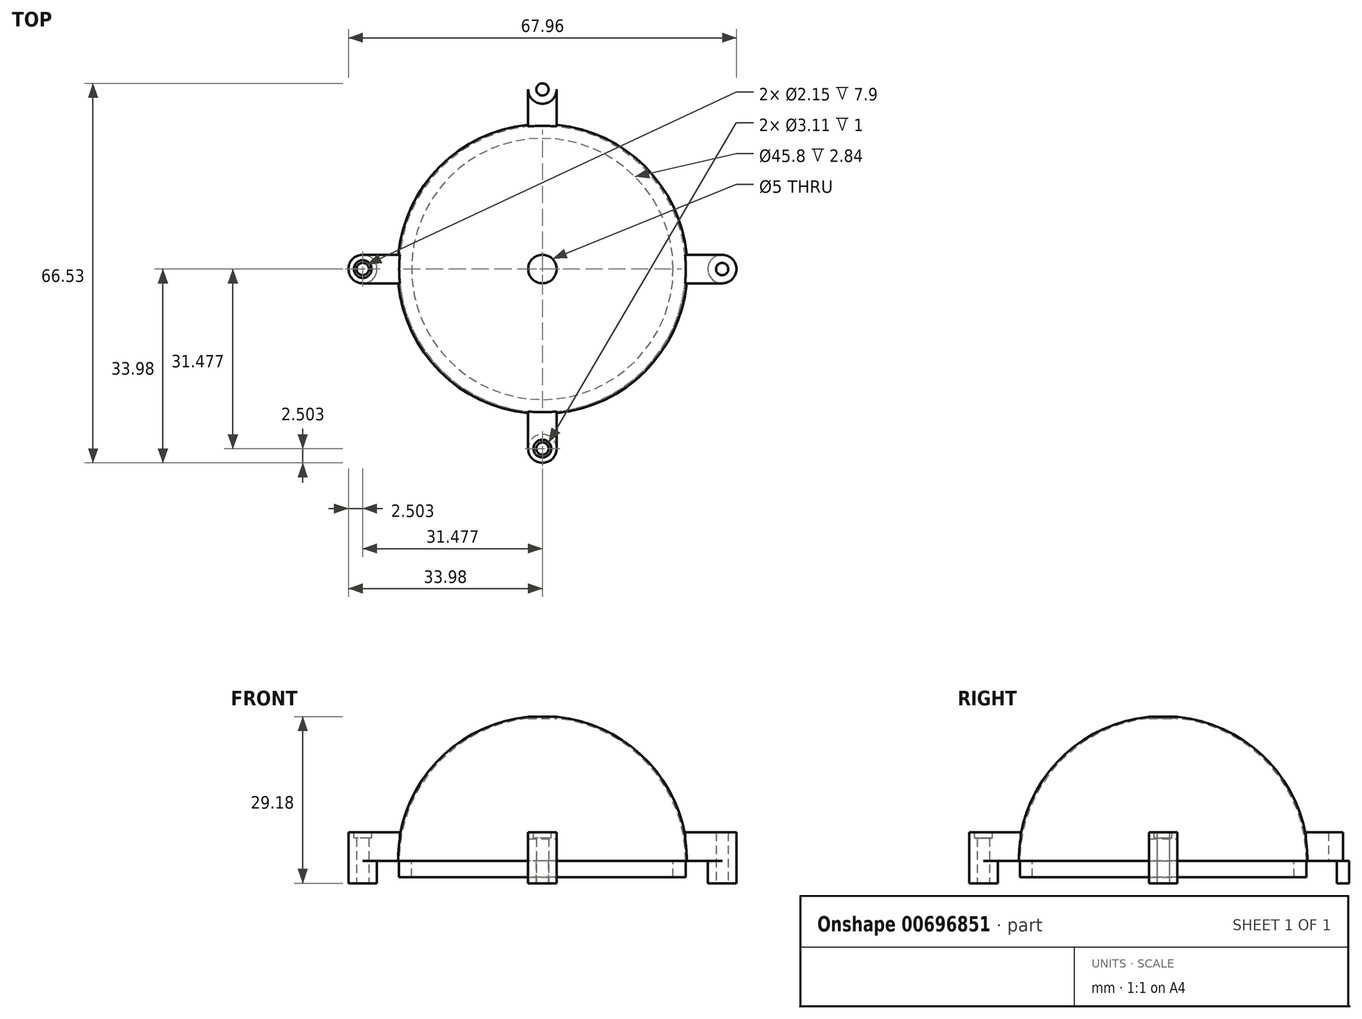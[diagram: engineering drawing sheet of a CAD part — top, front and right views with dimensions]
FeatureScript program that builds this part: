
annotation { "Feature Type Name" : "Feature", "Feature Type Description" : "" }
export const myFeature = defineFeature(function(context is Context, id is Id, definition is map)
    precondition{}
    {
        {
            var Q0;
            Q0=qCreatedBy(makeId("Top.planeOp"),FACE);
            var sketch = newSketch(context, id + "F0", { "sketchPlane" : qUnion([Q0])});
            skCircle(sketch, "E0", {"center": v(0, 0) * mm, "radius": 25.4 * mm});
            skCircle(sketch, "E1", {"center": v(0, 0) * mm, "radius": 22.9 * mm});
            skLineSegment(sketch, "E2", {"start": v(-75.08, 0) * mm, "end": v(76.97, 0) * mm});
            skLineSegment(sketch, "E3", {"start": v(-22.76, 2.5) * mm, "end": v(-31.48, 2.5) * mm});
            skLineSegment(sketch, "E4", {"start": v(-22.76, -2.5) * mm, "end": v(-31.48, -2.5) * mm});
            skCircle(sketch, "E5", {"center": v(-31.48, 0) * mm, "radius": 2.5 * mm});
            skPoint(sketch, "E6", {"position": v(-25.28, 2.5) * mm});
            skLineSegment(sketch, "E7.MirrorCS", {"start": v(22.76, 2.5) * mm, "end": v(31.48, 2.5) * mm});
            skLineSegment(sketch, "E8.MirrorCS", {"start": v(22.76, -2.5) * mm, "end": v(31.48, -2.5) * mm});
            skCircle(sketch, "E9.MirrorC", {"center": v(31.48, 0) * mm, "radius": 2.5 * mm});
            skLineSegment(sketch, "E10", {"start": v(0, 0) * mm, "end": v(95.02, -95.02) * mm, "construction": true});
            skLineSegment(sketch, "E11.MirrorCS", {"start": v(2.5, -22.76) * mm, "end": v(2.5, -31.48) * mm});
            skCircle(sketch, "E12.MirrorC", {"center": v(0, -31.48) * mm, "radius": 2.5 * mm});
            skLineSegment(sketch, "E13.MirrorCS", {"start": v(-2.5, -22.76) * mm, "end": v(-2.5, -31.48) * mm});
            skLineSegment(sketch, "E14.MirrorCS", {"start": v(2.5, 22.76) * mm, "end": v(2.5, 31.48) * mm});
            skCircle(sketch, "E15.MirrorC", {"center": v(0, 31.48) * mm, "radius": 2.5 * mm});
            skLineSegment(sketch, "E16.MirrorCS", {"start": v(-2.5, 22.76) * mm, "end": v(-2.5, 31.48) * mm});
            skCircle(sketch, "E17", {"center": v(0, -31.48) * mm, "radius": 1.07 * mm});
            skCircle(sketch, "E18.MirrorC", {"center": v(31.48, 0) * mm, "radius": 1.07 * mm});
            skCircle(sketch, "E19.MirrorC", {"center": v(0, 31.48) * mm, "radius": 1.07 * mm});
            skCircle(sketch, "E20.MirrorC", {"center": v(-31.48, 0) * mm, "radius": 1.07 * mm});
            skCircle(sketch, "E21", {"center": v(0, 0) * mm, "radius": 25.1 * mm});
            skCircle(sketch, "E22", {"center": v(0, 0) * mm, "radius": 2.5 * mm});
            skSolve(sketch);
        }
        {
            var Q0;
            {var subQ0=sQuery(id+"F0.wireOp",EDGE,"E7.MirrorCS");var subQ1=sQuery(id+"F0.wireOp",EDGE,"E0");var subQ2=makeQuery(id+"F0.imprint","INTERSECT",VERTEX,{"derivedFrom":[subQ1,subQ0]});Q0=makeQuery(id+"F0.imprint","IMPRINT",FACE,{"disambiguationData":[TD([[makeQuery(id+"F0.imprint","IMPRINT",EDGE,{"disambiguationData":[TD([[subQ2,-1.0]])],"derivedFrom":subQ1}),1.0]])]});}
            var Q1;
            {var subQ0=sQuery(id+"F0.wireOp",EDGE,"E7.MirrorCS");var subQ1=sQuery(id+"F0.wireOp",EDGE,"E0");var subQ2=makeQuery(id+"F0.imprint","INTERSECT",VERTEX,{"derivedFrom":[subQ1,subQ0]});Q1=makeQuery(id+"F0.imprint","IMPRINT",FACE,{"disambiguationData":[TD([[makeQuery(id+"F0.imprint","IMPRINT",EDGE,{"disambiguationData":[TD([[subQ2,1.0]])],"derivedFrom":subQ1}),1.0]])]});}
            var Q2;
            {var subQ0=sQuery(id+"F0.wireOp",EDGE,"E14.MirrorCS");var subQ1=sQuery(id+"F0.wireOp",EDGE,"E0");var subQ2=makeQuery(id+"F0.imprint","INTERSECT",VERTEX,{"derivedFrom":[subQ1,subQ0]});Q2=makeQuery(id+"F0.imprint","IMPRINT",FACE,{"disambiguationData":[TD([[makeQuery(id+"F0.imprint","IMPRINT",EDGE,{"disambiguationData":[TD([[subQ2,-1.0]])],"derivedFrom":subQ1}),1.0]])]});}
            var Q3;
            {var subQ0=sQuery(id+"F0.wireOp",EDGE,"E16.MirrorCS");var subQ1=sQuery(id+"F0.wireOp",EDGE,"E0");var subQ2=makeQuery(id+"F0.imprint","INTERSECT",VERTEX,{"derivedFrom":[subQ1,subQ0]});Q3=makeQuery(id+"F0.imprint","IMPRINT",FACE,{"disambiguationData":[TD([[makeQuery(id+"F0.imprint","IMPRINT",EDGE,{"disambiguationData":[TD([[subQ2,-1.0]])],"derivedFrom":subQ1}),1.0]])]});}
            var Q4;
            {var subQ0=sQuery(id+"F0.wireOp",EDGE,"E3");var subQ1=sQuery(id+"F0.wireOp",EDGE,"E0");var subQ2=makeQuery(id+"F0.imprint","INTERSECT",VERTEX,{"derivedFrom":[subQ1,subQ0]});Q4=makeQuery(id+"F0.imprint","IMPRINT",FACE,{"disambiguationData":[TD([[makeQuery(id+"F0.imprint","IMPRINT",EDGE,{"disambiguationData":[TD([[subQ2,-1.0]])],"derivedFrom":subQ1}),1.0]])]});}
            var Q5;
            Q5=sQuery(id+"F0.wireOp",EDGE,"E2");
            revolve(context, id + "F1", {"entities" : qUnion([Q0, Q1, Q2, Q3, Q4]), "axis" : qUnion([Q5]), "revolveType" : RevolveType.ONE_DIRECTION, "angle" : 180 * degree});
        }
        {
            var Q0;
            {var subQ0=sQuery(id+"F0.wireOp",EDGE,"E7.MirrorCS");var subQ1=sQuery(id+"F0.wireOp",EDGE,"E0");var subQ2=makeQuery(id+"F0.imprint","INTERSECT",VERTEX,{"derivedFrom":[subQ1,subQ0]});Q0=makeQuery(id+"F0.imprint","IMPRINT",FACE,{"disambiguationData":[TD([[makeQuery(id+"F0.imprint","IMPRINT",EDGE,{"disambiguationData":[TD([[subQ2,1.0]])],"derivedFrom":subQ1}),-1.0]])]});}
            var Q1;
            {var subQ0=sQuery(id+"F0.wireOp",EDGE,"E8.MirrorCS");var subQ1=sQuery(id+"F0.wireOp",EDGE,"E0");var subQ2=makeQuery(id+"F0.imprint","INTERSECT",VERTEX,{"derivedFrom":[subQ1,subQ0]});Q1=makeQuery(id+"F0.imprint","IMPRINT",FACE,{"disambiguationData":[TD([[makeQuery(id+"F0.imprint","IMPRINT",EDGE,{"disambiguationData":[TD([[subQ2,-1.0]])],"derivedFrom":subQ1}),-1.0]])]});}
            var Q2;
            {var subQ0=sQuery(id+"F0.wireOp",EDGE,"E9.MirrorC");var subQ1=sQuery(id+"F0.wireOp",EDGE,"E2");var subQ2=makeQuery(id+"F0.imprint","INTERSECT",VERTEX,{"disambiguationData":[OD(0.0)],"derivedFrom":[subQ1,subQ0]});Q2=makeQuery(id+"F0.imprint","IMPRINT",FACE,{"disambiguationData":[TD([[makeQuery(id+"F0.imprint","IMPRINT",EDGE,{"disambiguationData":[TD([[subQ2,1.0]])],"derivedFrom":subQ1}),1.0]])]});}
            var Q3;
            {var subQ0=sQuery(id+"F0.wireOp",EDGE,"E9.MirrorC");var subQ1=sQuery(id+"F0.wireOp",EDGE,"E2");var subQ2=makeQuery(id+"F0.imprint","INTERSECT",VERTEX,{"disambiguationData":[OD(0.0)],"derivedFrom":[subQ1,subQ0]});Q3=makeQuery(id+"F0.imprint","IMPRINT",FACE,{"disambiguationData":[TD([[makeQuery(id+"F0.imprint","IMPRINT",EDGE,{"disambiguationData":[TD([[subQ2,1.0]])],"derivedFrom":subQ1}),-1.0]])]});}
            var Q4;
            {var subQ0=sQuery(id+"F0.wireOp",EDGE,"E7.MirrorCS");var subQ1=sQuery(id+"F0.wireOp",EDGE,"E0");var subQ2=makeQuery(id+"F0.imprint","INTERSECT",VERTEX,{"derivedFrom":[subQ1,subQ0]});Q4=makeQuery(id+"F0.imprint","IMPRINT",FACE,{"disambiguationData":[TD([[makeQuery(id+"F0.imprint","IMPRINT",EDGE,{"disambiguationData":[TD([[subQ2,1.0]])],"derivedFrom":subQ1}),1.0]])]});}
            var Q5;
            {var subQ0=sQuery(id+"F0.wireOp",EDGE,"E8.MirrorCS");var subQ1=sQuery(id+"F0.wireOp",EDGE,"E0");var subQ2=makeQuery(id+"F0.imprint","INTERSECT",VERTEX,{"derivedFrom":[subQ1,subQ0]});Q5=makeQuery(id+"F0.imprint","IMPRINT",FACE,{"disambiguationData":[TD([[makeQuery(id+"F0.imprint","IMPRINT",EDGE,{"disambiguationData":[TD([[subQ2,-1.0]])],"derivedFrom":subQ1}),1.0]])]});}
            var Q6;
            {var subQ0=sQuery(id+"F0.wireOp",EDGE,"E14.MirrorCS");var subQ1=sQuery(id+"F0.wireOp",EDGE,"E0");var subQ2=makeQuery(id+"F0.imprint","INTERSECT",VERTEX,{"derivedFrom":[subQ1,subQ0]});Q6=makeQuery(id+"F0.imprint","IMPRINT",FACE,{"disambiguationData":[TD([[makeQuery(id+"F0.imprint","IMPRINT",EDGE,{"disambiguationData":[TD([[subQ2,-1.0]])],"derivedFrom":subQ1}),1.0]])]});}
            var Q7;
            {var subQ0=sQuery(id+"F0.wireOp",EDGE,"E14.MirrorCS");var subQ1=sQuery(id+"F0.wireOp",EDGE,"E0");var subQ2=makeQuery(id+"F0.imprint","INTERSECT",VERTEX,{"derivedFrom":[subQ1,subQ0]});Q7=makeQuery(id+"F0.imprint","IMPRINT",FACE,{"disambiguationData":[TD([[makeQuery(id+"F0.imprint","IMPRINT",EDGE,{"disambiguationData":[TD([[subQ2,-1.0]])],"derivedFrom":subQ1}),-1.0]])]});}
            var Q8;
            {var subQ0=sQuery(id+"F0.wireOp",EDGE,"E15.MirrorC");var subQ1=makeQuery(id+"F0.imprint","INTERSECT",VERTEX,{"derivedFrom":[sQuery(id+"F0.wireOp",EDGE,"E14.MirrorCS"),subQ0]});Q8=makeQuery(id+"F0.imprint","IMPRINT",FACE,{"disambiguationData":[TD([[makeQuery(id+"F0.imprint","IMPRINT",EDGE,{"disambiguationData":[TD([[subQ1,1.0]])],"derivedFrom":subQ0}),-1.0]])]});}
            var Q9;
            {var subQ0=sQuery(id+"F0.wireOp",EDGE,"E3");var subQ1=sQuery(id+"F0.wireOp",EDGE,"E0");var subQ2=makeQuery(id+"F0.imprint","INTERSECT",VERTEX,{"derivedFrom":[subQ1,subQ0]});Q9=makeQuery(id+"F0.imprint","IMPRINT",FACE,{"disambiguationData":[TD([[makeQuery(id+"F0.imprint","IMPRINT",EDGE,{"disambiguationData":[TD([[subQ2,-1.0]])],"derivedFrom":subQ1}),-1.0]])]});}
            var Q10;
            {var subQ0=sQuery(id+"F0.wireOp",EDGE,"E5");var subQ1=sQuery(id+"F0.wireOp",EDGE,"E2");var subQ2=makeQuery(id+"F0.imprint","INTERSECT",VERTEX,{"disambiguationData":[OD(0.0)],"derivedFrom":[subQ1,subQ0]});Q10=makeQuery(id+"F0.imprint","IMPRINT",FACE,{"disambiguationData":[TD([[makeQuery(id+"F0.imprint","IMPRINT",EDGE,{"disambiguationData":[TD([[subQ2,-1.0]])],"derivedFrom":subQ1}),1.0]])]});}
            var Q11;
            {var subQ0=sQuery(id+"F0.wireOp",EDGE,"E5");var subQ1=sQuery(id+"F0.wireOp",EDGE,"E2");var subQ2=makeQuery(id+"F0.imprint","INTERSECT",VERTEX,{"disambiguationData":[OD(0.0)],"derivedFrom":[subQ1,subQ0]});Q11=makeQuery(id+"F0.imprint","IMPRINT",FACE,{"disambiguationData":[TD([[makeQuery(id+"F0.imprint","IMPRINT",EDGE,{"disambiguationData":[TD([[subQ2,-1.0]])],"derivedFrom":subQ1}),-1.0]])]});}
            var Q12;
            {var subQ0=sQuery(id+"F0.wireOp",EDGE,"E4");var subQ1=sQuery(id+"F0.wireOp",EDGE,"E0");var subQ2=makeQuery(id+"F0.imprint","INTERSECT",VERTEX,{"derivedFrom":[subQ1,subQ0]});Q12=makeQuery(id+"F0.imprint","IMPRINT",FACE,{"disambiguationData":[TD([[makeQuery(id+"F0.imprint","IMPRINT",EDGE,{"disambiguationData":[TD([[subQ2,1.0]])],"derivedFrom":subQ1}),-1.0]])]});}
            var Q13;
            {var subQ0=sQuery(id+"F0.wireOp",EDGE,"E4");var subQ1=sQuery(id+"F0.wireOp",EDGE,"E0");var subQ2=makeQuery(id+"F0.imprint","INTERSECT",VERTEX,{"derivedFrom":[subQ1,subQ0]});Q13=makeQuery(id+"F0.imprint","IMPRINT",FACE,{"disambiguationData":[TD([[makeQuery(id+"F0.imprint","IMPRINT",EDGE,{"disambiguationData":[TD([[subQ2,1.0]])],"derivedFrom":subQ1}),1.0]])]});}
            var Q14;
            {var subQ0=sQuery(id+"F0.wireOp",EDGE,"E3");var subQ1=sQuery(id+"F0.wireOp",EDGE,"E0");var subQ2=makeQuery(id+"F0.imprint","INTERSECT",VERTEX,{"derivedFrom":[subQ1,subQ0]});Q14=makeQuery(id+"F0.imprint","IMPRINT",FACE,{"disambiguationData":[TD([[makeQuery(id+"F0.imprint","IMPRINT",EDGE,{"disambiguationData":[TD([[subQ2,-1.0]])],"derivedFrom":subQ1}),1.0]])]});}
            var Q15;
            {var subQ0=sQuery(id+"F0.wireOp",EDGE,"E12.MirrorC");var subQ1=makeQuery(id+"F0.imprint","INTERSECT",VERTEX,{"derivedFrom":[sQuery(id+"F0.wireOp",EDGE,"E11.MirrorCS"),subQ0]});Q15=makeQuery(id+"F0.imprint","IMPRINT",FACE,{"disambiguationData":[TD([[makeQuery(id+"F0.imprint","IMPRINT",EDGE,{"disambiguationData":[TD([[subQ1,1.0]])],"derivedFrom":subQ0}),1.0]])]});}
            var Q16;
            {var subQ0=sQuery(id+"F0.wireOp",EDGE,"E13.MirrorCS");var subQ1=sQuery(id+"F0.wireOp",EDGE,"E0");var subQ2=makeQuery(id+"F0.imprint","INTERSECT",VERTEX,{"derivedFrom":[subQ1,subQ0]});Q16=makeQuery(id+"F0.imprint","IMPRINT",FACE,{"disambiguationData":[TD([[makeQuery(id+"F0.imprint","IMPRINT",EDGE,{"disambiguationData":[TD([[subQ2,-1.0]])],"derivedFrom":subQ1}),-1.0]])]});}
            var Q17;
            {var subQ0=sQuery(id+"F0.wireOp",EDGE,"E13.MirrorCS");var subQ1=sQuery(id+"F0.wireOp",EDGE,"E0");var subQ2=makeQuery(id+"F0.imprint","INTERSECT",VERTEX,{"derivedFrom":[subQ1,subQ0]});Q17=makeQuery(id+"F0.imprint","IMPRINT",FACE,{"disambiguationData":[TD([[makeQuery(id+"F0.imprint","IMPRINT",EDGE,{"disambiguationData":[TD([[subQ2,-1.0]])],"derivedFrom":subQ1}),1.0]])]});}
            extrude(context, id + "F2", {"entities" : qUnion([Q0, Q1, Q2, Q3, Q4, Q5, Q6, Q7, Q8, Q9, Q10, Q11, Q12, Q13, Q14, Q15, Q16, Q17]), "depth" : 5 * mm, "offsetDistance" : 25 * mm});
        }
        {
            var Q0;
            {var subQ0=sQuery(id+"F0.wireOp",EDGE,"E7.MirrorCS");var subQ1=sQuery(id+"F0.wireOp",EDGE,"E1");var subQ2=makeQuery(id+"F0.imprint","INTERSECT",VERTEX,{"derivedFrom":[subQ1,subQ0]});Q0=makeQuery(id+"F0.imprint","IMPRINT",FACE,{"disambiguationData":[TD([[makeQuery(id+"F0.imprint","IMPRINT",EDGE,{"disambiguationData":[TD([[subQ2,-1.0]])],"derivedFrom":subQ1}),-1.0]])]});}
            var Q1;
            {var subQ0=sQuery(id+"F0.wireOp",EDGE,"E7.MirrorCS");var subQ1=sQuery(id+"F0.wireOp",EDGE,"E1");var subQ2=makeQuery(id+"F0.imprint","INTERSECT",VERTEX,{"derivedFrom":[subQ1,subQ0]});Q1=makeQuery(id+"F0.imprint","IMPRINT",FACE,{"disambiguationData":[TD([[makeQuery(id+"F0.imprint","IMPRINT",EDGE,{"disambiguationData":[TD([[subQ2,1.0]])],"derivedFrom":subQ1}),-1.0]])]});}
            var Q2;
            {var subQ0=sQuery(id+"F0.wireOp",EDGE,"E8.MirrorCS");var subQ1=sQuery(id+"F0.wireOp",EDGE,"E1");var subQ2=makeQuery(id+"F0.imprint","INTERSECT",VERTEX,{"derivedFrom":[subQ1,subQ0]});Q2=makeQuery(id+"F0.imprint","IMPRINT",FACE,{"disambiguationData":[TD([[makeQuery(id+"F0.imprint","IMPRINT",EDGE,{"disambiguationData":[TD([[subQ2,-1.0]])],"derivedFrom":subQ1}),-1.0]])]});}
            var Q3;
            {var subQ0=sQuery(id+"F0.wireOp",EDGE,"E8.MirrorCS");var subQ1=sQuery(id+"F0.wireOp",EDGE,"E1");var subQ2=makeQuery(id+"F0.imprint","INTERSECT",VERTEX,{"derivedFrom":[subQ1,subQ0]});Q3=makeQuery(id+"F0.imprint","IMPRINT",FACE,{"disambiguationData":[TD([[makeQuery(id+"F0.imprint","IMPRINT",EDGE,{"disambiguationData":[TD([[subQ2,1.0]])],"derivedFrom":subQ1}),-1.0]])]});}
            var Q4;
            {var subQ0=sQuery(id+"F0.wireOp",EDGE,"E11.MirrorCS");var subQ1=sQuery(id+"F0.wireOp",EDGE,"E1");var subQ2=makeQuery(id+"F0.imprint","INTERSECT",VERTEX,{"derivedFrom":[subQ1,subQ0]});Q4=makeQuery(id+"F0.imprint","IMPRINT",FACE,{"disambiguationData":[TD([[makeQuery(id+"F0.imprint","IMPRINT",EDGE,{"disambiguationData":[TD([[subQ2,1.0]])],"derivedFrom":subQ1}),-1.0]])]});}
            var Q5;
            {var subQ0=sQuery(id+"F0.wireOp",EDGE,"E4");var subQ1=sQuery(id+"F0.wireOp",EDGE,"E1");var subQ2=makeQuery(id+"F0.imprint","INTERSECT",VERTEX,{"derivedFrom":[subQ1,subQ0]});Q5=makeQuery(id+"F0.imprint","IMPRINT",FACE,{"disambiguationData":[TD([[makeQuery(id+"F0.imprint","IMPRINT",EDGE,{"disambiguationData":[TD([[subQ2,-1.0]])],"derivedFrom":subQ1}),-1.0]])]});}
            var Q6;
            {var subQ0=sQuery(id+"F0.wireOp",EDGE,"E4");var subQ1=sQuery(id+"F0.wireOp",EDGE,"E1");var subQ2=makeQuery(id+"F0.imprint","INTERSECT",VERTEX,{"derivedFrom":[subQ1,subQ0]});Q6=makeQuery(id+"F0.imprint","IMPRINT",FACE,{"disambiguationData":[TD([[makeQuery(id+"F0.imprint","IMPRINT",EDGE,{"disambiguationData":[TD([[subQ2,1.0]])],"derivedFrom":subQ1}),-1.0]])]});}
            var Q7;
            {var subQ0=sQuery(id+"F0.wireOp",EDGE,"E3");var subQ1=sQuery(id+"F0.wireOp",EDGE,"E1");var subQ2=makeQuery(id+"F0.imprint","INTERSECT",VERTEX,{"derivedFrom":[subQ1,subQ0]});Q7=makeQuery(id+"F0.imprint","IMPRINT",FACE,{"disambiguationData":[TD([[makeQuery(id+"F0.imprint","IMPRINT",EDGE,{"disambiguationData":[TD([[subQ2,-1.0]])],"derivedFrom":subQ1}),-1.0]])]});}
            var Q8;
            {var subQ0=sQuery(id+"F0.wireOp",EDGE,"E3");var subQ1=sQuery(id+"F0.wireOp",EDGE,"E1");var subQ2=makeQuery(id+"F0.imprint","INTERSECT",VERTEX,{"derivedFrom":[subQ1,subQ0]});Q8=makeQuery(id+"F0.imprint","IMPRINT",FACE,{"disambiguationData":[TD([[makeQuery(id+"F0.imprint","IMPRINT",EDGE,{"disambiguationData":[TD([[subQ2,1.0]])],"derivedFrom":subQ1}),-1.0]])]});}
            var Q9;
            {var subQ0=sQuery(id+"F0.wireOp",EDGE,"E14.MirrorCS");var subQ1=sQuery(id+"F0.wireOp",EDGE,"E1");var subQ2=makeQuery(id+"F0.imprint","INTERSECT",VERTEX,{"derivedFrom":[subQ1,subQ0]});Q9=makeQuery(id+"F0.imprint","IMPRINT",FACE,{"disambiguationData":[TD([[makeQuery(id+"F0.imprint","IMPRINT",EDGE,{"disambiguationData":[TD([[subQ2,-1.0]])],"derivedFrom":subQ1}),-1.0]])]});}
            extrude(context, id + "F3", {"entities" : qUnion([Q0, Q1, Q2, Q3, Q4, Q5, Q6, Q7, Q8, Q9]), "operationType" : NewBodyOperationType.ADD, "oppositeDirection" : true, "depth" : 2.84 * mm, "offsetDistance" : 25 * mm});
        }
        {
            var Q0;
            {var subQ0=sQuery(id+"F0.wireOp",EDGE,"E5");var subQ2=sQuery(id+"F0.wireOp",EDGE,"E2");var subQ6=makeQuery(id+"F0.imprint","INTERSECT",VERTEX,{"disambiguationData":[OD(0.0)],"derivedFrom":[subQ2,subQ0]});Q0=makeQuery(id+"F0.imprint","IMPRINT",FACE,{"disambiguationData":[TD([[makeQuery(id+"F0.imprint","IMPRINT",EDGE,{"disambiguationData":[TD([[subQ6,-1.0]])],"derivedFrom":subQ2}),1.0]])]});}
            var Q1;
            {var subQ0=sQuery(id+"F0.wireOp",EDGE,"E5");var subQ2=sQuery(id+"F0.wireOp",EDGE,"E2");var subQ3=makeQuery(id+"F0.imprint","INTERSECT",VERTEX,{"disambiguationData":[OD(0.0)],"derivedFrom":[subQ2,subQ0]});Q1=makeQuery(id+"F0.imprint","IMPRINT",FACE,{"disambiguationData":[TD([[makeQuery(id+"F0.imprint","IMPRINT",EDGE,{"disambiguationData":[TD([[subQ3,-1.0]])],"derivedFrom":subQ2}),-1.0]])]});}
            var Q2;
            Q2=makeQuery(id+"F0.imprint","IMPRINT",FACE,{"disambiguationData":[TD([[makeQuery(id+"F0.imprint","IMPRINT",EDGE,{"derivedFrom":sQuery(id+"F0.wireOp",EDGE,"E17")}),-1.0]])]});
            var Q3;
            Q3=makeQuery(id+"F0.imprint","IMPRINT",FACE,{"disambiguationData":[TD([[makeQuery(id+"F0.imprint","IMPRINT",EDGE,{"derivedFrom":sQuery(id+"F0.wireOp",EDGE,"E19.MirrorC")}),1.0]])]});
            var Q4;
            {var subQ0=sQuery(id+"F0.wireOp",EDGE,"E9.MirrorC");var subQ2=sQuery(id+"F0.wireOp",EDGE,"E2");var subQ3=makeQuery(id+"F0.imprint","INTERSECT",VERTEX,{"disambiguationData":[OD(1.0)],"derivedFrom":[subQ2,subQ0]});Q4=makeQuery(id+"F0.imprint","IMPRINT",FACE,{"disambiguationData":[TD([[makeQuery(id+"F0.imprint","IMPRINT",EDGE,{"disambiguationData":[TD([[subQ3,-1.0]])],"derivedFrom":subQ2}),1.0]])]});}
            var Q5;
            {var subQ0=sQuery(id+"F0.wireOp",EDGE,"E9.MirrorC");var subQ2=sQuery(id+"F0.wireOp",EDGE,"E2");var subQ4=makeQuery(id+"F0.imprint","INTERSECT",VERTEX,{"disambiguationData":[OD(1.0)],"derivedFrom":[subQ2,subQ0]});Q5=makeQuery(id+"F0.imprint","IMPRINT",FACE,{"disambiguationData":[TD([[makeQuery(id+"F0.imprint","IMPRINT",EDGE,{"disambiguationData":[TD([[subQ4,-1.0]])],"derivedFrom":subQ2}),-1.0]])]});}
            extrude(context, id + "F4", {"entities" : qUnion([Q0, Q1, Q2, Q3, Q4, Q5]), "operationType" : NewBodyOperationType.ADD, "oppositeDirection" : true, "depth" : 3.9 * mm, "offsetDistance" : 25 * mm});
        }
        {
            var Q0;
            Q0=makeQuery(id+"F2.opExtrude","CAP_FACE",FACE,{"disambiguationData":[OSD([sQuery(id+"F0.wireOp",EDGE,"E3"),sQuery(id+"F0.wireOp",EDGE,"E4"),sQuery(id+"F0.wireOp",EDGE,"E5"),sQuery(id+"F0.wireOp",EDGE,"E20.MirrorC"),sQuery(id+"F0.wireOp",EDGE,"E21")])],"isStart":false});
            var sketch = newSketch(context, id + "F5", { "sketchPlane" : qUnion([Q0])});
            skCircle(sketch, "E23", {"center": v(-31.48, 0) * mm, "radius": 1.55 * mm});
            skCircle(sketch, "E24.MirrorC", {"center": v(31.48, 0) * mm, "radius": 1.55 * mm});
            skCircle(sketch, "E25.MirrorC", {"center": v(0, -31.48) * mm, "radius": 1.55 * mm});
            skCircle(sketch, "E26.MirrorC", {"center": v(0, 31.48) * mm, "radius": 1.55 * mm});
            skSolve(sketch);
        }
        {
            var Q0;
            Q0=makeQuery(id+"F5.imprint","IMPRINT",FACE,{"disambiguationData":[TD([[makeQuery(id+"F5.imprint","IMPRINT",EDGE,{"derivedFrom":sQuery(id+"F5.wireOp",EDGE,"E25.MirrorC")}),1.0]])]});
            var Q1;
            Q1=makeQuery(id+"F5.imprint","IMPRINT",FACE,{"disambiguationData":[TD([[makeQuery(id+"F5.imprint","IMPRINT",EDGE,{"derivedFrom":sQuery(id+"F5.wireOp",EDGE,"E23")}),1.0]])]});
            var Q2;
            Q2=makeQuery(id+"F5.imprint","IMPRINT",FACE,{"disambiguationData":[TD([[makeQuery(id+"F5.imprint","IMPRINT",EDGE,{"derivedFrom":sQuery(id+"F5.wireOp",EDGE,"E26.MirrorC")}),-1.0]])]});
            var Q3;
            Q3=makeQuery(id+"F5.imprint","IMPRINT",FACE,{"disambiguationData":[TD([[makeQuery(id+"F5.imprint","IMPRINT",EDGE,{"derivedFrom":sQuery(id+"F5.wireOp",EDGE,"E24.MirrorC")}),-1.0]])]});
            extrude(context, id + "F6", {"entities" : qUnion([Q0, Q1, Q2, Q3]), "operationType" : NewBodyOperationType.REMOVE, "oppositeDirection" : true, "depth" : 1 * mm, "offsetDistance" : 25 * mm});
        }
        {
            var Q0;
            {var subQ0=sQuery(id+"F0.wireOp",EDGE,"E22");var subQ1=sQuery(id+"F0.wireOp",EDGE,"E2");var subQ2=makeQuery(id+"F0.imprint","INTERSECT",VERTEX,{"disambiguationData":[OD(0.0)],"derivedFrom":[subQ1,subQ0]});Q0=makeQuery(id+"F0.imprint","IMPRINT",FACE,{"disambiguationData":[TD([[makeQuery(id+"F0.imprint","IMPRINT",EDGE,{"disambiguationData":[TD([[subQ2,-1.0]])],"derivedFrom":subQ1}),1.0]])]});}
            var Q1;
            {var subQ0=sQuery(id+"F0.wireOp",EDGE,"E22");var subQ1=sQuery(id+"F0.wireOp",EDGE,"E2");var subQ2=makeQuery(id+"F0.imprint","INTERSECT",VERTEX,{"disambiguationData":[OD(0.0)],"derivedFrom":[subQ1,subQ0]});Q1=makeQuery(id+"F0.imprint","IMPRINT",FACE,{"disambiguationData":[TD([[makeQuery(id+"F0.imprint","IMPRINT",EDGE,{"disambiguationData":[TD([[subQ2,-1.0]])],"derivedFrom":subQ1}),-1.0]])]});}
            extrude(context, id + "F7", {"entities" : qUnion([Q0, Q1]), "operationType" : NewBodyOperationType.REMOVE, "depth" : 50 * mm, "offsetDistance" : 25 * mm});
        }
    });
